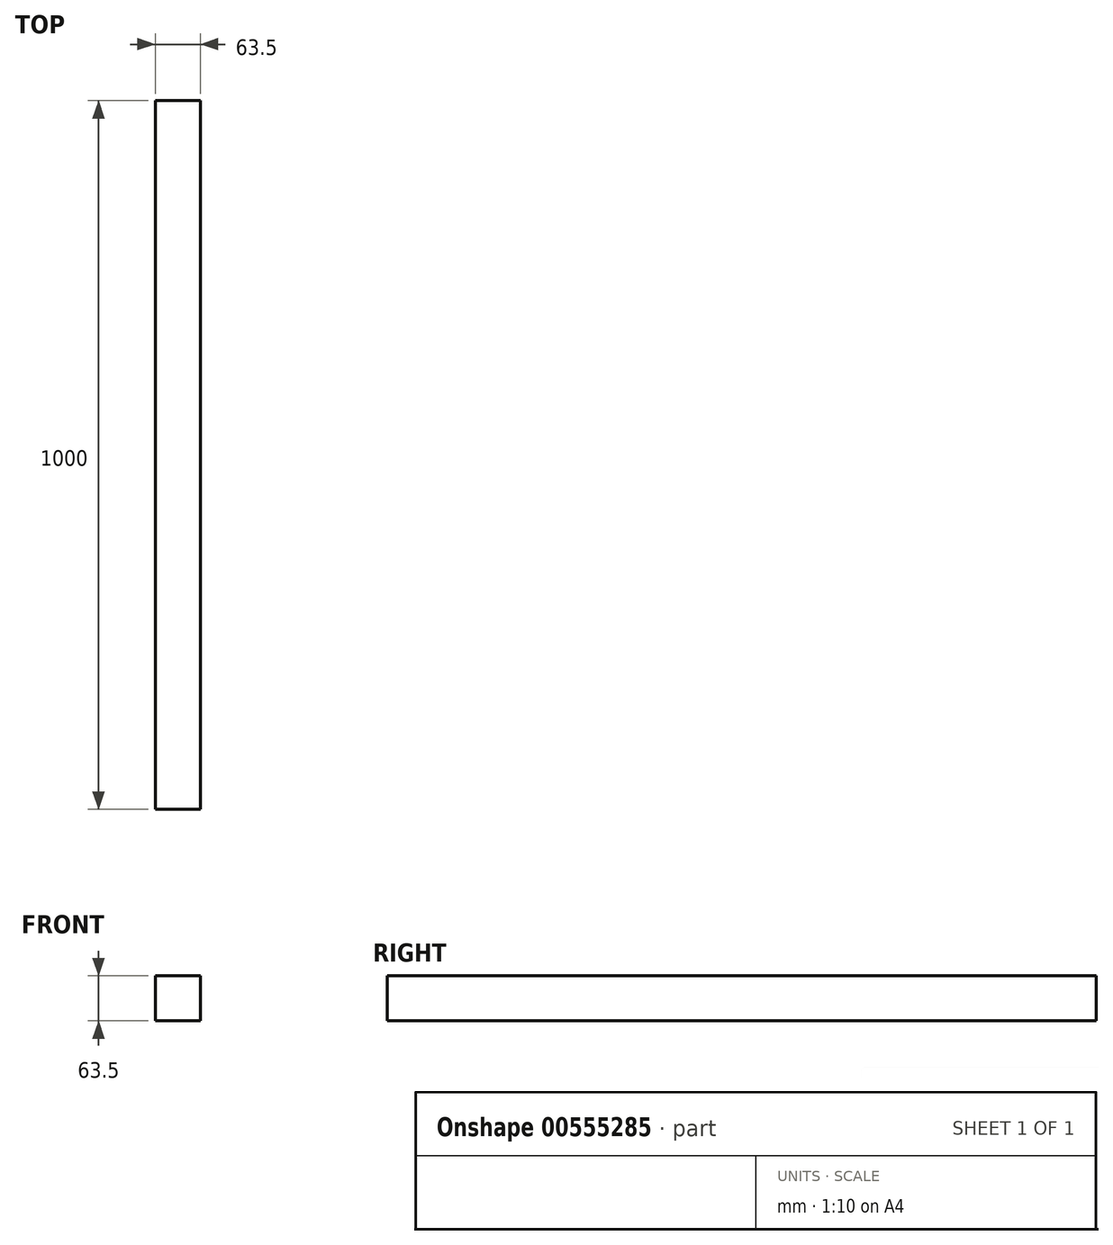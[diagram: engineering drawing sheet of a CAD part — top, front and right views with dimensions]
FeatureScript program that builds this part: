
annotation { "Feature Type Name" : "Feature", "Feature Type Description" : "" }
export const myFeature = defineFeature(function(context is Context, id is Id, definition is map)
    precondition{}
    {
        {
            var Q0;
            Q0=qCreatedBy(makeId("Front.planeOp"),FACE);
            var sketch = newSketch(context, id + "F0", { "sketchPlane" : qUnion([Q0])});
            skLineSegment(sketch, "E0.bottom", {"start": v(-55.03, 41.65) * mm, "end": v(8.47, 41.65) * mm});
            skLineSegment(sketch, "E0.top", {"start": v(-55.03, -21.85) * mm, "end": v(8.47, -21.85) * mm});
            skLineSegment(sketch, "E0.left", {"start": v(-55.03, 41.65) * mm, "end": v(-55.03, -21.85) * mm});
            skLineSegment(sketch, "E0.right", {"start": v(8.47, 41.65) * mm, "end": v(8.47, -21.85) * mm});
            skSolve(sketch);
        }
        {
            var Q0;
            Q0 = qSketchRegion(id + "F0", true);
            extrude(context, id + "F1", {"entities" : qUnion([Q0]), "depth" : 1000 * mm, "offsetDistance" : 25.4 * mm});
        }
    });
